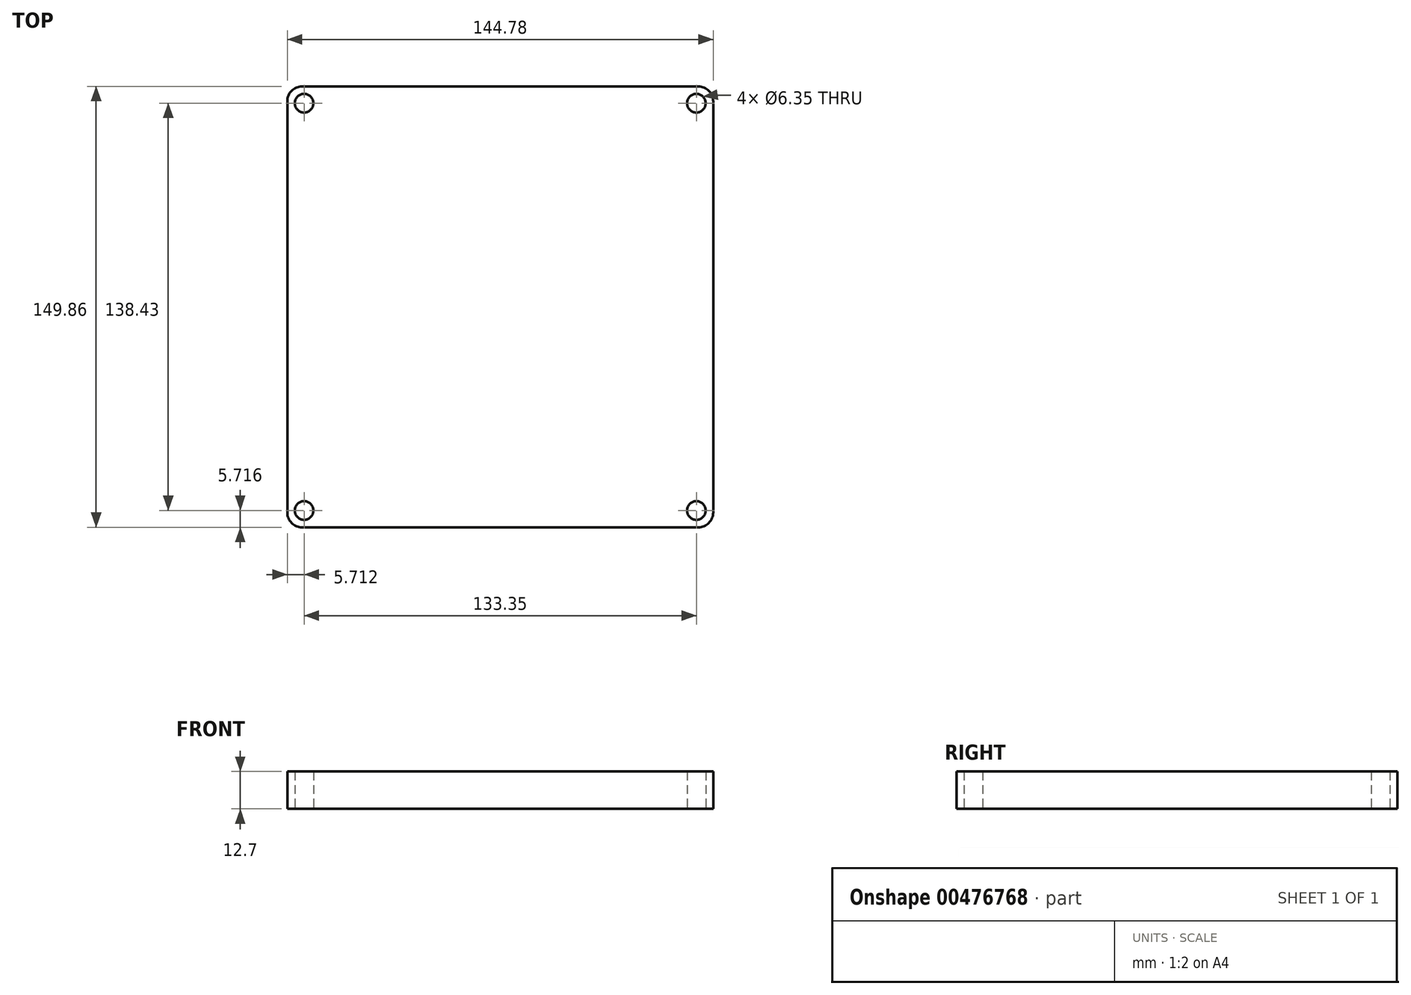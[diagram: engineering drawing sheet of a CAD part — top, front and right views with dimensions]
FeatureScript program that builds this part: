
annotation { "Feature Type Name" : "Feature", "Feature Type Description" : "" }
export const myFeature = defineFeature(function(context is Context, id is Id, definition is map)
    precondition{}
    {
        {
            var Q0;
            Q0=qCreatedBy(makeId("Top.planeOp"),FACE);
            var sketch = newSketch(context, id + "F0", { "sketchPlane" : qUnion([Q0])});
            skLineSegment(sketch, "E0.bottom", {"start": v(-70.71, 69.26) * mm, "end": v(74.07, 69.26) * mm});
            skLineSegment(sketch, "E0.top", {"start": v(-70.71, -80.6) * mm, "end": v(74.07, -80.6) * mm});
            skLineSegment(sketch, "E0.left", {"start": v(-70.71, 69.26) * mm, "end": v(-70.71, -80.6) * mm});
            skLineSegment(sketch, "E0.right", {"start": v(74.07, 69.26) * mm, "end": v(74.07, -80.6) * mm});
            skCircle(sketch, "E1", {"center": v(-65, 63.55) * mm, "radius": 3.18 * mm});
            skPoint(sketch, "E2", {"position": v(-65, 66.72) * mm});
            skPoint(sketch, "E3", {"position": v(-68.17, 63.55) * mm});
            skLineSegment(sketch, "E4", {"start": v(1.68, 69.26) * mm, "end": v(1.68, -83.9) * mm, "construction": true});
            skPoint(sketch, "E4.endSnap0", {"position": v(1.68, -80.6) * mm});
            skLineSegment(sketch, "E5", {"start": v(-70.71, -5.67) * mm, "end": v(93.15, -5.67) * mm, "construction": true});
            skCircle(sketch, "E6.MirrorC", {"center": v(-65, -74.88) * mm, "radius": 3.18 * mm});
            skCircle(sketch, "E7.MirrorC", {"center": v(68.35, -74.88) * mm, "radius": 3.18 * mm});
            skCircle(sketch, "E8.MirrorC", {"center": v(68.35, 63.55) * mm, "radius": 3.18 * mm});
            skSolve(sketch);
        }
        {
            var Q0;
            Q0=makeQuery(id+"F0.imprint","IMPRINT",FACE,{"disambiguationData":[TD([[makeQuery(id+"F0.imprint","IMPRINT",EDGE,{"derivedFrom":sQuery(id+"F0.wireOp",EDGE,"E0.bottom")}),-1.0]])]});
            extrude(context, id + "F1", {"entities" : qUnion([Q0]), "depth" : 12.7 * mm});
        }
        {
            var Q0;
            Q0=makeQuery(id+"F1.opExtrude","SWEPT_EDGE",EDGE,{"disambiguationData":[OSD([sQuery(id+"F0.wireOp",EDGE,"E0.bottom"),sQuery(id+"F0.wireOp",EDGE,"E0.right")])]});
            var Q1;
            Q1=makeQuery(id+"F1.opExtrude","SWEPT_EDGE",EDGE,{"disambiguationData":[OSD([sQuery(id+"F0.wireOp",EDGE,"E0.top"),sQuery(id+"F0.wireOp",EDGE,"E0.right")])]});
            var Q2;
            Q2=makeQuery(id+"F1.opExtrude","SWEPT_EDGE",EDGE,{"disambiguationData":[OSD([sQuery(id+"F0.wireOp",EDGE,"E0.bottom"),sQuery(id+"F0.wireOp",EDGE,"E0.left")])]});
            var Q3;
            Q3=makeQuery(id+"F1.opExtrude","SWEPT_EDGE",EDGE,{"disambiguationData":[OSD([sQuery(id+"F0.wireOp",EDGE,"E0.top"),sQuery(id+"F0.wireOp",EDGE,"E0.left")])]});
            fillet(context, id + "F2", {"entities" : qUnion([Q0, Q1, Q2, Q3]), "radius" : 5.08 * mm, "tangentPropagation" : true, "allowEdgeOverflow" : false});
        }
    });
